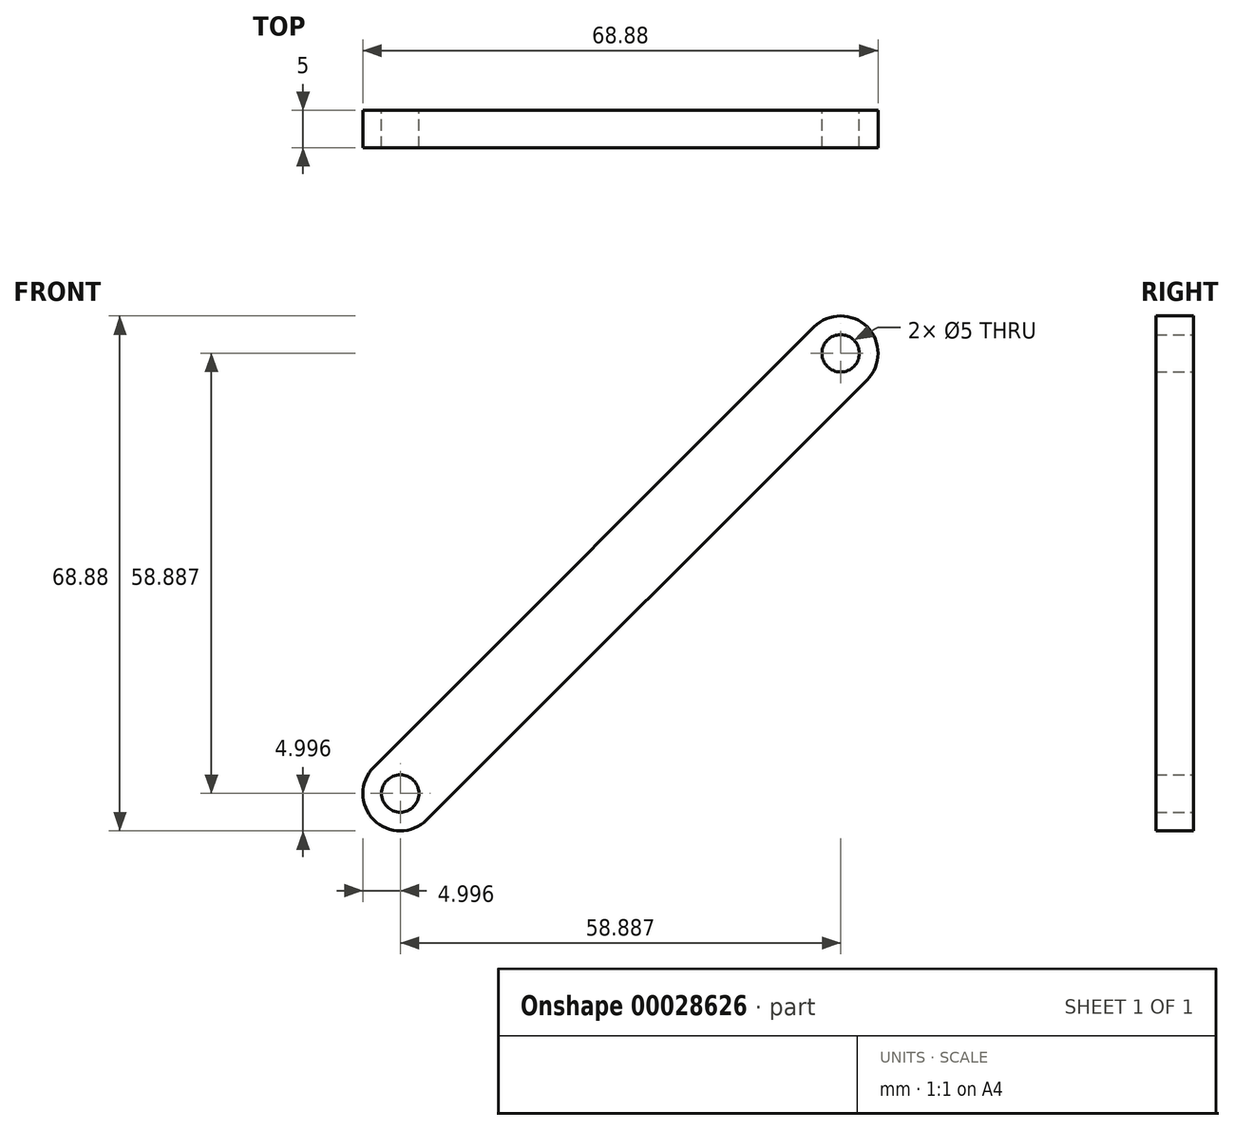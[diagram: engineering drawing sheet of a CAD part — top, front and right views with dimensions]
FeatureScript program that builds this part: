
annotation { "Feature Type Name" : "Feature", "Feature Type Description" : "" }
export const myFeature = defineFeature(function(context is Context, id is Id, definition is map)
    precondition{}
    {
        {
            var Q0;
            Q0=qCreatedBy(makeId("Front.planeOp"),FACE);
            var sketch = newSketch(context, id + "F0", { "sketchPlane" : qUnion([Q0])});
            skLineSegment(sketch, "E0", {"start": v(0, 0) * mm, "end": v(32.98, 32.98) * mm});
            skLineSegment(sketch, "E1", {"start": v(0, 0) * mm, "end": v(-32.98, -32.98) * mm});
            skLineSegment(sketch, "E2", {"start": v(32.98, 32.98) * mm, "end": v(29.44, 36.51) * mm});
            skLineSegment(sketch, "E3", {"start": v(32.98, 32.98) * mm, "end": v(36.51, 29.44) * mm});
            skLineSegment(sketch, "E4", {"start": v(-32.98, -32.98) * mm, "end": v(-36.51, -29.44) * mm});
            skLineSegment(sketch, "E5", {"start": v(-32.98, -32.98) * mm, "end": v(-29.44, -36.51) * mm});
            skLineSegment(sketch, "E6", {"start": v(29.44, 36.51) * mm, "end": v(-36.51, -29.44) * mm});
            skLineSegment(sketch, "E7", {"start": v(36.51, 29.44) * mm, "end": v(-29.44, -36.51) * mm});
            skCircle(sketch, "E8", {"center": v(29.44, 29.44) * mm, "radius": 2.5 * mm});
            skCircle(sketch, "E9", {"center": v(29.44, 29.44) * mm, "radius": 5 * mm});
            skCircle(sketch, "E10", {"center": v(-29.44, -29.44) * mm, "radius": 5 * mm});
            skCircle(sketch, "E11", {"center": v(-29.44, -29.44) * mm, "radius": 2.5 * mm});
            skSolve(sketch);
        }
        {
            var Q0;
            {var subQ1=sQuery(id+"F0.wireOp",EDGE,"E1");var subQ6=sQuery(id+"F0.wireOp",EDGE,"E0");var subQ12=makeQuery(id+"F0.imprint","INTERSECT",VERTEX,{"derivedFrom":[subQ6,subQ1]});Q0=makeQuery(id+"F0.imprint","IMPRINT",FACE,{"disambiguationData":[TD([[makeQuery(id+"F0.imprint","IMPRINT",EDGE,{"disambiguationData":[TD([[subQ12,-1.0]])],"derivedFrom":subQ6}),1.0]])]});}
            var Q1;
            {var subQ1=sQuery(id+"F0.wireOp",EDGE,"E1");var subQ6=sQuery(id+"F0.wireOp",EDGE,"E0");var subQ12=makeQuery(id+"F0.imprint","INTERSECT",VERTEX,{"derivedFrom":[subQ6,subQ1]});Q1=makeQuery(id+"F0.imprint","IMPRINT",FACE,{"disambiguationData":[TD([[makeQuery(id+"F0.imprint","IMPRINT",EDGE,{"disambiguationData":[TD([[subQ12,-1.0]])],"derivedFrom":subQ6}),-1.0]])]});}
            var Q2;
            {var subQ0=sQuery(id+"F0.wireOp",EDGE,"E9");var subQ1=makeQuery(id+"F0.imprint","INTERSECT",VERTEX,{"derivedFrom":[sQuery(id+"F0.wireOp",EDGE,"E7"),subQ0]});Q2=makeQuery(id+"F0.imprint","IMPRINT",FACE,{"disambiguationData":[TD([[makeQuery(id+"F0.imprint","IMPRINT",EDGE,{"disambiguationData":[TD([[subQ1,1.0]])],"derivedFrom":subQ0}),1.0]])]});}
            var Q3;
            {var subQ0=sQuery(id+"F0.wireOp",EDGE,"E9");var subQ1=makeQuery(id+"F0.imprint","INTERSECT",VERTEX,{"derivedFrom":[sQuery(id+"F0.wireOp",EDGE,"E6"),subQ0]});Q3=makeQuery(id+"F0.imprint","IMPRINT",FACE,{"disambiguationData":[TD([[makeQuery(id+"F0.imprint","IMPRINT",EDGE,{"disambiguationData":[TD([[subQ1,-1.0]])],"derivedFrom":subQ0}),1.0]])]});}
            var Q4;
            {var subQ0=sQuery(id+"F0.wireOp",EDGE,"E10");var subQ1=makeQuery(id+"F0.imprint","INTERSECT",VERTEX,{"derivedFrom":[sQuery(id+"F0.wireOp",EDGE,"E6"),subQ0]});Q4=makeQuery(id+"F0.imprint","IMPRINT",FACE,{"disambiguationData":[TD([[makeQuery(id+"F0.imprint","IMPRINT",EDGE,{"disambiguationData":[TD([[subQ1,1.0]])],"derivedFrom":subQ0}),1.0]])]});}
            var Q5;
            {var subQ0=sQuery(id+"F0.wireOp",EDGE,"E10");var subQ3=makeQuery(id+"F0.imprint","INTERSECT",VERTEX,{"derivedFrom":[sQuery(id+"F0.wireOp",EDGE,"E7"),subQ0]});Q5=makeQuery(id+"F0.imprint","IMPRINT",FACE,{"disambiguationData":[TD([[makeQuery(id+"F0.imprint","IMPRINT",EDGE,{"disambiguationData":[TD([[subQ3,-1.0]])],"derivedFrom":subQ0}),1.0]])]});}
            extrude(context, id + "F1", {"entities" : qUnion([Q0, Q1, Q2, Q3, Q4, Q5]), "endBound" : BoundingType.SYMMETRIC, "depth" : 5 * mm});
        }
    });
